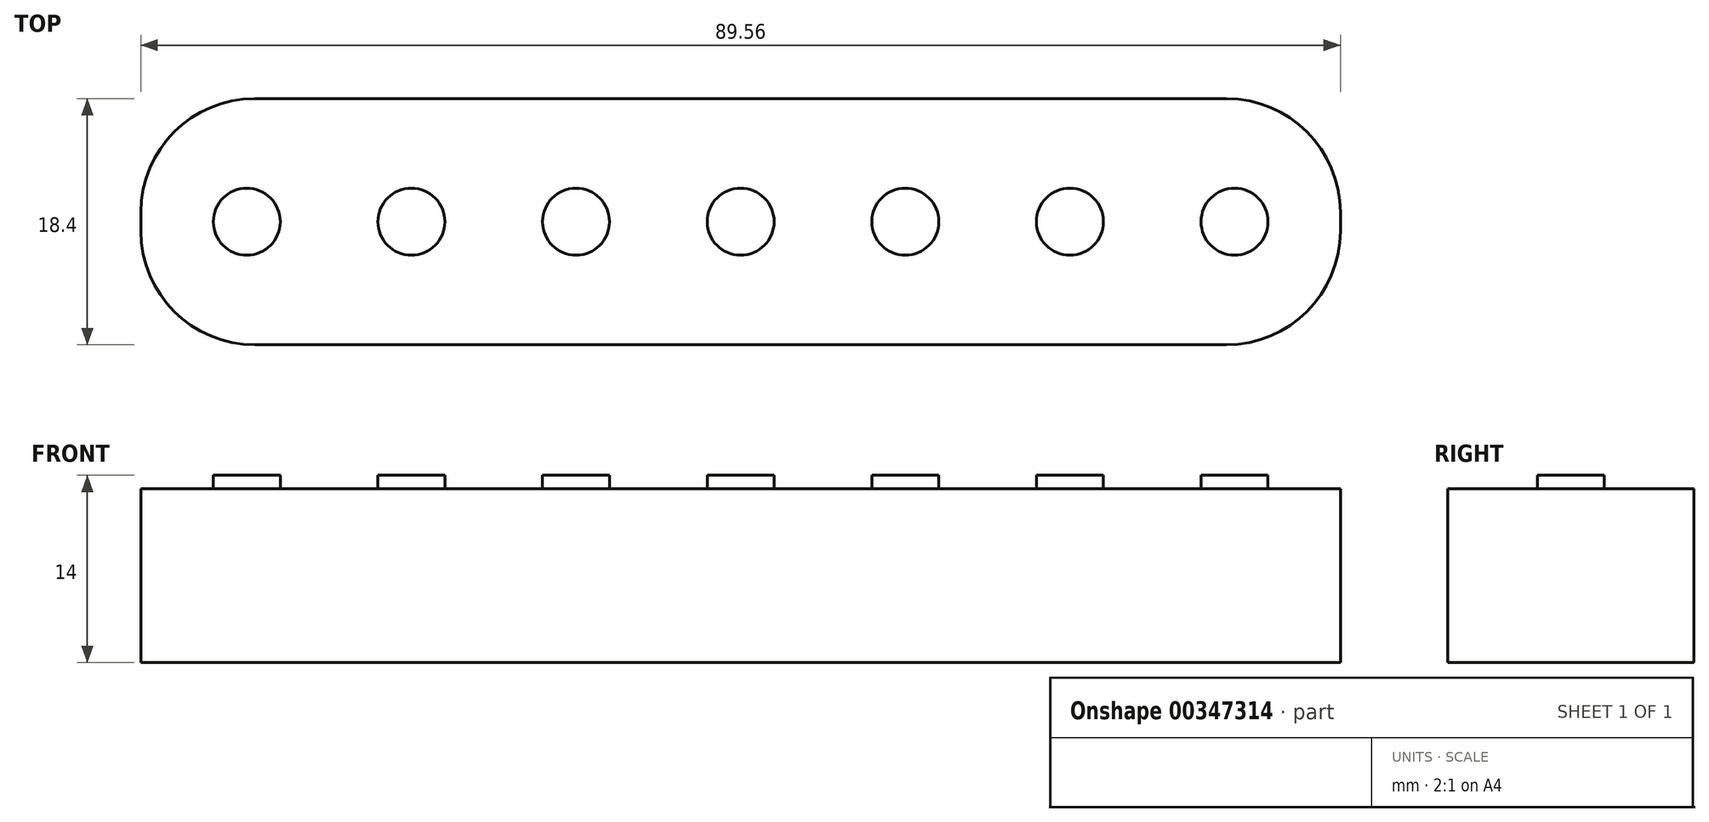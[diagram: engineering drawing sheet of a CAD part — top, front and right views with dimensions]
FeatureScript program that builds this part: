
annotation { "Feature Type Name" : "Feature", "Feature Type Description" : "" }
export const myFeature = defineFeature(function(context is Context, id is Id, definition is map)
    precondition{}
    {
        {
            var Q0;
            Q0=qCreatedBy(makeId("Top.planeOp"),FACE);
            var sketch = newSketch(context, id + "F0", { "sketchPlane" : qUnion([Q0])});
            skLineSegment(sketch, "E0.bottom", {"start": v(-36.27, 9.2) * mm, "end": v(36.27, 9.2) * mm});
            skLineSegment(sketch, "E0.top", {"start": v(-36.27, -9.2) * mm, "end": v(36.27, -9.2) * mm});
            skLineSegment(sketch, "E0.left", {"start": v(-44.78, 0.7) * mm, "end": v(-44.78, -0.7) * mm});
            skLineSegment(sketch, "E0.right", {"start": v(44.78, 0.7) * mm, "end": v(44.78, -0.7) * mm});
            skPoint(sketch, "E0.middle", {"position": v(0, 0) * mm});
            skLineSegment(sketch, "E1", {"start": v(-44.78, 0) * mm, "end": v(44.78, 0) * mm, "construction": true});
            skLineSegment(sketch, "E2", {"start": v(0, 9.2) * mm, "end": v(0, -9.2) * mm, "construction": true});
            skPoint(sketch, "E3.visualSharp", {"position": v(-44.78, 9.2) * mm});
            skArc(sketch, "E3.filletArc", {"start": v(-36.27, 9.2) * mm, "mid": v(-42.29, 6.71) * mm, "end": v(-44.77, 0.7) * mm});
            skPoint(sketch, "E4.visualSharp", {"position": v(-44.78, -9.2) * mm});
            skArc(sketch, "E4.filletArc", {"start": v(-44.78, -0.7) * mm, "mid": v(-42.29, -6.71) * mm, "end": v(-36.27, -9.2) * mm});
            skPoint(sketch, "E5.visualSharp", {"position": v(44.78, -9.2) * mm});
            skArc(sketch, "E5.filletArc", {"start": v(36.27, -9.2) * mm, "mid": v(42.29, -6.71) * mm, "end": v(44.77, -0.7) * mm});
            skPoint(sketch, "E6.visualSharp", {"position": v(44.78, 9.2) * mm});
            skArc(sketch, "E6.filletArc", {"start": v(44.78, 0.7) * mm, "mid": v(42.29, 6.71) * mm, "end": v(36.27, 9.2) * mm});
            skCircle(sketch, "E7", {"center": v(-36.87, 0) * mm, "radius": 2.5 * mm});
            skCircle(sketch, "E8.1.0.0", {"center": v(-24.58, 0) * mm, "radius": 2.5 * mm});
            skCircle(sketch, "E8.2.0.0", {"center": v(-12.3, 0) * mm, "radius": 2.5 * mm});
            skCircle(sketch, "E8.3.0.0", {"center": v(0, 0) * mm, "radius": 2.5 * mm});
            skCircle(sketch, "E8.4.0.0", {"center": v(12.3, 0) * mm, "radius": 2.5 * mm});
            skCircle(sketch, "E8.5.0.0", {"center": v(24.58, 0) * mm, "radius": 2.5 * mm});
            skCircle(sketch, "E8.6.0.0", {"center": v(36.88, 0) * mm, "radius": 2.5 * mm});
            skLineSegment(sketch, "E8.direction1", {"start": v(-36.87, 0) * mm, "end": v(-24.58, 0) * mm, "construction": true});
            skSolve(sketch);
        }
        {
            var Q0;
            Q0=makeQuery(id+"F0.imprint","IMPRINT",FACE,{"disambiguationData":[TD([[makeQuery(id+"F0.imprint","IMPRINT",EDGE,{"derivedFrom":sQuery(id+"F0.wireOp",EDGE,"E0.bottom")}),-1.0]])]});
            extrude(context, id + "F1", {"entities" : qUnion([Q0]), "depth" : 13 * mm});
        }
        {
            var Q0;
            Q0=makeQuery(id+"F0.imprint","IMPRINT",FACE,{"disambiguationData":[TD([[makeQuery(id+"F0.imprint","IMPRINT",EDGE,{"derivedFrom":sQuery(id+"F0.wireOp",EDGE,"E7")}),1.0]])]});
            var Q1;
            Q1=makeQuery(id+"F0.imprint","IMPRINT",FACE,{"disambiguationData":[TD([[makeQuery(id+"F0.imprint","IMPRINT",EDGE,{"derivedFrom":sQuery(id+"F0.wireOp",EDGE,"E8.1.0.0")}),1.0]])]});
            var Q2;
            Q2=makeQuery(id+"F0.imprint","IMPRINT",FACE,{"disambiguationData":[TD([[makeQuery(id+"F0.imprint","IMPRINT",EDGE,{"derivedFrom":sQuery(id+"F0.wireOp",EDGE,"E8.2.0.0")}),1.0]])]});
            var Q3;
            Q3=makeQuery(id+"F0.imprint","IMPRINT",FACE,{"disambiguationData":[TD([[makeQuery(id+"F0.imprint","IMPRINT",EDGE,{"derivedFrom":sQuery(id+"F0.wireOp",EDGE,"E8.3.0.0")}),1.0]])]});
            var Q4;
            Q4=makeQuery(id+"F0.imprint","IMPRINT",FACE,{"disambiguationData":[TD([[makeQuery(id+"F0.imprint","IMPRINT",EDGE,{"derivedFrom":sQuery(id+"F0.wireOp",EDGE,"E8.4.0.0")}),1.0]])]});
            var Q5;
            Q5=makeQuery(id+"F0.imprint","IMPRINT",FACE,{"disambiguationData":[TD([[makeQuery(id+"F0.imprint","IMPRINT",EDGE,{"derivedFrom":sQuery(id+"F0.wireOp",EDGE,"E8.6.0.0")}),1.0]])]});
            var Q6;
            Q6=makeQuery(id+"F0.imprint","IMPRINT",FACE,{"disambiguationData":[TD([[makeQuery(id+"F0.imprint","IMPRINT",EDGE,{"derivedFrom":sQuery(id+"F0.wireOp",EDGE,"E8.5.0.0")}),1.0]])]});
            extrude(context, id + "F2", {"entities" : qUnion([Q0, Q1, Q2, Q3, Q4, Q5, Q6]), "operationType" : NewBodyOperationType.ADD, "depth" : 14 * mm});
        }
    });
